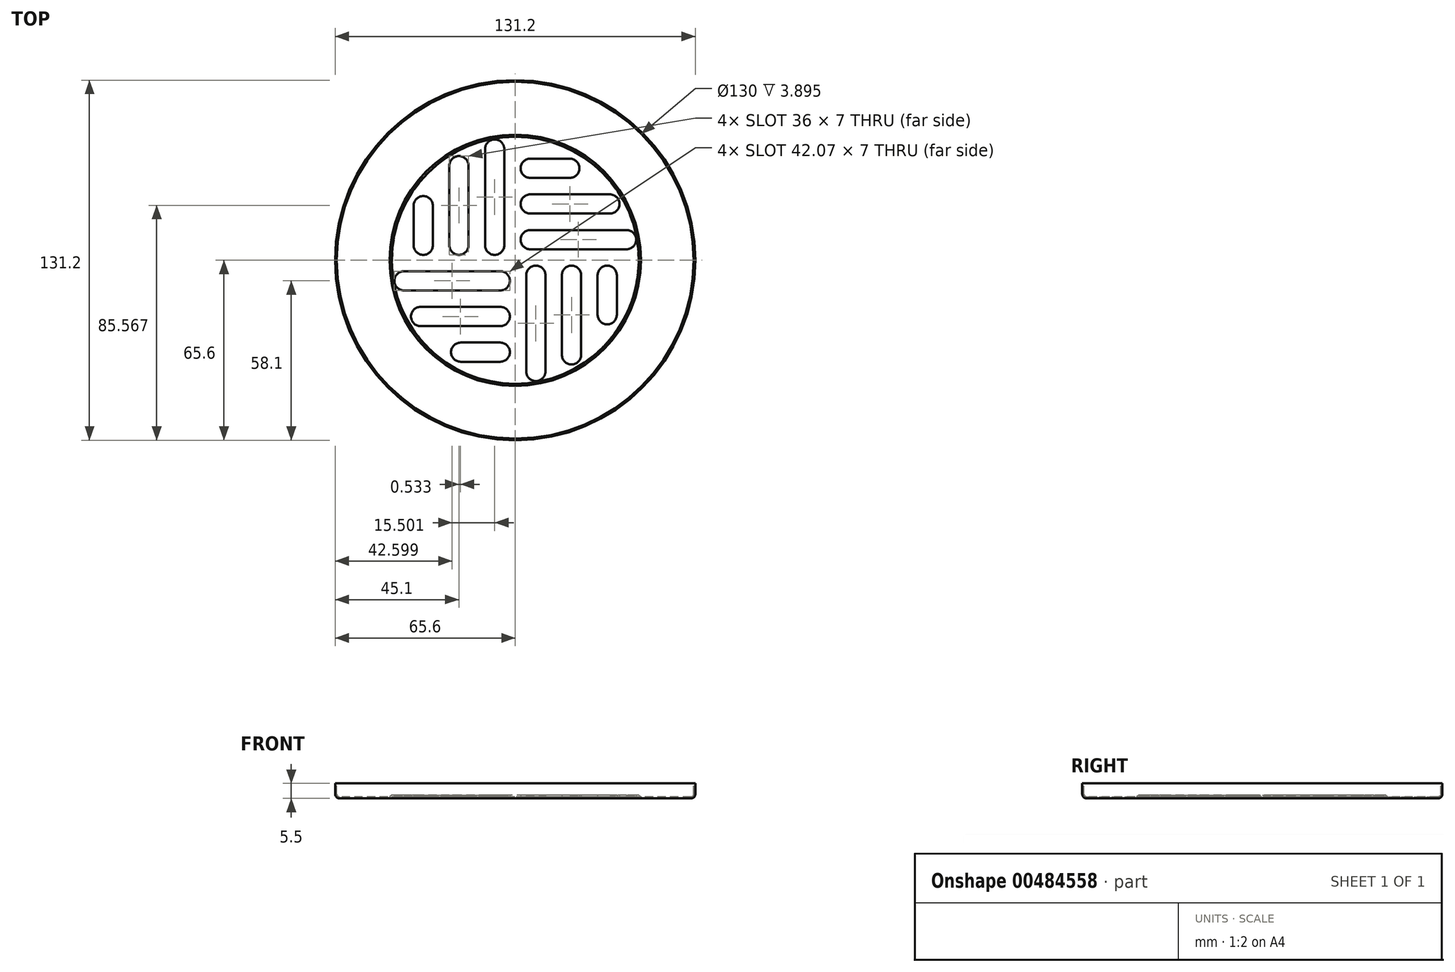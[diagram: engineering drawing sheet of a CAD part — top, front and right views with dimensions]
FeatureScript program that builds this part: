
annotation { "Feature Type Name" : "Feature", "Feature Type Description" : "" }
export const myFeature = defineFeature(function(context is Context, id is Id, definition is map)
    precondition{}
    {
        {
            var Q0;
            Q0=qCreatedBy(makeId("Front.planeOp"),FACE);
            var sketch = newSketch(context, id + "F0", { "sketchPlane" : qUnion([Q0])});
            skLineSegment(sketch, "E0", {"start": v(-65, 4.9) * mm, "end": v(-65, 1) * mm});
            skLineSegment(sketch, "E1", {"start": v(-64, 0) * mm, "end": v(-45.79, 0) * mm});
            skLineSegment(sketch, "E2", {"start": v(-45.79, 0) * mm, "end": v(-45, 0.6) * mm});
            skLineSegment(sketch, "E3", {"start": v(-45, 0.6) * mm, "end": v(0, 0.6) * mm});
            skPoint(sketch, "E4.visualSharp", {"position": v(-65, 0) * mm});
            skArc(sketch, "E4.filletArc", {"start": v(-65, 1) * mm, "mid": v(-64.7, 0.3) * mm, "end": v(-64, 0) * mm});
            skLineSegment(sketch, "E5.0", {"start": v(-44.8, 0) * mm, "end": v(0, 0) * mm});
            skLineSegment(sketch, "E5.1", {"start": v(-65.6, 4.9) * mm, "end": v(-65.6, 1) * mm});
            skArc(sketch, "E5.2", {"start": v(-65.6, 1) * mm, "mid": v(-65.13, -0.13) * mm, "end": v(-64, -0.6) * mm});
            skLineSegment(sketch, "E5.3", {"start": v(-64, -0.6) * mm, "end": v(-45.58, -0.6) * mm});
            skLineSegment(sketch, "E5.4", {"start": v(-45.58, -0.6) * mm, "end": v(-44.8, 0) * mm});
            skLineSegment(sketch, "E6", {"start": v(-65.6, 4.9) * mm, "end": v(-65, 4.9) * mm});
            skLineSegment(sketch, "E7", {"start": v(0, 0) * mm, "end": v(0, 0.6) * mm});
            skLineSegment(sketch, "E8", {"start": v(0, 16) * mm, "end": v(0, -11.03) * mm, "construction": true});
            skSolve(sketch);
        }
        {
            var Q0;
            Q0=makeQuery(id+"F0.imprint","IMPRINT",FACE,{"disambiguationData":[TD([[makeQuery(id+"F0.imprint","IMPRINT",EDGE,{"derivedFrom":sQuery(id+"F0.wireOp",EDGE,"E0")}),-1.0]])]});
            var Q1;
            Q1=sQuery(id+"F0.wireOp",EDGE,"E8");
            revolve(context, id + "F1", {"entities" : qUnion([Q0]), "axis" : qUnion([Q1]), "revolveType" : RevolveType.FULL});
        }
        {
            var Q0;
            Q0=qCreatedBy(makeId("Top.planeOp"),FACE);
            var sketch = newSketch(context, id + "F2", { "sketchPlane" : qUnion([Q0])});
            skLineSegment(sketch, "E9.left", {"start": v(-11, 40.53) * mm, "end": v(-11, 5.47) * mm});
            skLineSegment(sketch, "E9.right", {"start": v(-4, 40.47) * mm, "end": v(-4, 5.47) * mm});
            skLineSegment(sketch, "E10.left", {"start": v(-24, 34.47) * mm, "end": v(-24, 5.47) * mm});
            skLineSegment(sketch, "E10.right", {"start": v(-17, 34.47) * mm, "end": v(-17, 5.47) * mm});
            skLineSegment(sketch, "E11.left", {"start": v(-37, 19.87) * mm, "end": v(-37, 5.47) * mm});
            skLineSegment(sketch, "E11.right", {"start": v(-30, 19.87) * mm, "end": v(-30, 5.47) * mm});
            skArc(sketch, "E12", {"start": v(-37, 19.87) * mm, "mid": v(-33.5, 23.37) * mm, "end": v(-30, 19.87) * mm});
            skArc(sketch, "E13", {"start": v(-30, 5.47) * mm, "mid": v(-33.5, 1.97) * mm, "end": v(-37, 5.47) * mm});
            skArc(sketch, "E14", {"start": v(-24, 5.47) * mm, "mid": v(-20.5, 1.97) * mm, "end": v(-17, 5.47) * mm});
            skArc(sketch, "E15", {"start": v(-17, 34.47) * mm, "mid": v(-20.5, 37.97) * mm, "end": v(-24, 34.47) * mm});
            skArc(sketch, "E16", {"start": v(-11, 40.53) * mm, "mid": v(-7.47, 44.03) * mm, "end": v(-4, 40.47) * mm});
            skArc(sketch, "E17", {"start": v(-11, 5.47) * mm, "mid": v(-7.5, 1.97) * mm, "end": v(-4, 5.47) * mm});
            skLineSegment(sketch, "E18.1.0", {"start": v(-40.47, -4) * mm, "end": v(-5.47, -4) * mm});
            skArc(sketch, "E18.1.1", {"start": v(-5.47, -11) * mm, "mid": v(-1.97, -7.5) * mm, "end": v(-5.47, -4) * mm});
            skLineSegment(sketch, "E18.1.2", {"start": v(-40.53, -11) * mm, "end": v(-5.47, -11) * mm});
            skArc(sketch, "E18.1.3", {"start": v(-40.53, -11) * mm, "mid": v(-44.03, -7.47) * mm, "end": v(-40.47, -4) * mm});
            skLineSegment(sketch, "E18.1.4", {"start": v(-34.47, -17) * mm, "end": v(-5.47, -17) * mm});
            skArc(sketch, "E18.1.5", {"start": v(-34.47, -17) * mm, "mid": v(-37.97, -20.5) * mm, "end": v(-34.47, -24) * mm});
            skLineSegment(sketch, "E18.1.6", {"start": v(-34.47, -24) * mm, "end": v(-5.47, -24) * mm});
            skArc(sketch, "E18.1.7", {"start": v(-5.47, -24) * mm, "mid": v(-1.97, -20.5) * mm, "end": v(-5.47, -17) * mm});
            skLineSegment(sketch, "E18.1.8", {"start": v(-19.87, -30) * mm, "end": v(-5.47, -30) * mm});
            skArc(sketch, "E18.1.9", {"start": v(-19.87, -37) * mm, "mid": v(-23.37, -33.5) * mm, "end": v(-19.87, -30) * mm});
            skLineSegment(sketch, "E18.1.10", {"start": v(-19.87, -37) * mm, "end": v(-5.47, -37) * mm});
            skArc(sketch, "E18.1.11", {"start": v(-5.47, -30) * mm, "mid": v(-1.97, -33.5) * mm, "end": v(-5.47, -37) * mm});
            skLineSegment(sketch, "E18.2.0", {"start": v(4, -40.47) * mm, "end": v(4, -5.47) * mm});
            skArc(sketch, "E18.2.1", {"start": v(11, -5.47) * mm, "mid": v(7.5, -1.97) * mm, "end": v(4, -5.47) * mm});
            skLineSegment(sketch, "E18.2.2", {"start": v(11, -40.53) * mm, "end": v(11, -5.47) * mm});
            skArc(sketch, "E18.2.3", {"start": v(11, -40.53) * mm, "mid": v(7.47, -44.03) * mm, "end": v(4, -40.47) * mm});
            skLineSegment(sketch, "E18.2.4", {"start": v(17, -34.47) * mm, "end": v(17, -5.47) * mm});
            skArc(sketch, "E18.2.5", {"start": v(17, -34.47) * mm, "mid": v(20.5, -37.97) * mm, "end": v(24, -34.47) * mm});
            skLineSegment(sketch, "E18.2.6", {"start": v(24, -34.47) * mm, "end": v(24, -5.47) * mm});
            skArc(sketch, "E18.2.7", {"start": v(24, -5.47) * mm, "mid": v(20.5, -1.97) * mm, "end": v(17, -5.47) * mm});
            skLineSegment(sketch, "E18.2.8", {"start": v(30, -19.87) * mm, "end": v(30, -5.47) * mm});
            skArc(sketch, "E18.2.9", {"start": v(37, -19.87) * mm, "mid": v(33.5, -23.37) * mm, "end": v(30, -19.87) * mm});
            skLineSegment(sketch, "E18.2.10", {"start": v(37, -19.87) * mm, "end": v(37, -5.47) * mm});
            skArc(sketch, "E18.2.11", {"start": v(30, -5.47) * mm, "mid": v(33.5, -1.97) * mm, "end": v(37, -5.47) * mm});
            skLineSegment(sketch, "E18.3.0", {"start": v(40.47, 4) * mm, "end": v(5.47, 4) * mm});
            skArc(sketch, "E18.3.1", {"start": v(5.47, 11) * mm, "mid": v(1.97, 7.5) * mm, "end": v(5.47, 4) * mm});
            skLineSegment(sketch, "E18.3.2", {"start": v(40.53, 11) * mm, "end": v(5.47, 11) * mm});
            skArc(sketch, "E18.3.3", {"start": v(40.53, 11) * mm, "mid": v(44.03, 7.47) * mm, "end": v(40.47, 4) * mm});
            skLineSegment(sketch, "E18.3.4", {"start": v(34.47, 17) * mm, "end": v(5.47, 17) * mm});
            skArc(sketch, "E18.3.5", {"start": v(34.47, 17) * mm, "mid": v(37.97, 20.5) * mm, "end": v(34.47, 24) * mm});
            skLineSegment(sketch, "E18.3.6", {"start": v(34.47, 24) * mm, "end": v(5.47, 24) * mm});
            skArc(sketch, "E18.3.7", {"start": v(5.47, 24) * mm, "mid": v(1.97, 20.5) * mm, "end": v(5.47, 17) * mm});
            skLineSegment(sketch, "E18.3.8", {"start": v(19.87, 30) * mm, "end": v(5.47, 30) * mm});
            skArc(sketch, "E18.3.9", {"start": v(19.87, 37) * mm, "mid": v(23.37, 33.5) * mm, "end": v(19.87, 30) * mm});
            skLineSegment(sketch, "E18.3.10", {"start": v(19.87, 37) * mm, "end": v(5.47, 37) * mm});
            skArc(sketch, "E18.3.11", {"start": v(5.47, 30) * mm, "mid": v(1.97, 33.5) * mm, "end": v(5.47, 37) * mm});
            skPoint(sketch, "E18.center", {"position": v(0, 0) * mm});
            skSolve(sketch);
        }
        {
            var Q0;
            Q0=makeQuery(id+"F2.imprint","IMPRINT",FACE,{"disambiguationData":[TD([[makeQuery(id+"F2.imprint","IMPRINT",EDGE,{"derivedFrom":sQuery(id+"F2.wireOp",EDGE,"E18.1.0")}),-1.0]])]});
            var Q1;
            Q1=makeQuery(id+"F2.imprint","IMPRINT",FACE,{"disambiguationData":[TD([[makeQuery(id+"F2.imprint","IMPRINT",EDGE,{"derivedFrom":sQuery(id+"F2.wireOp",EDGE,"E18.1.4")}),-1.0]])]});
            var Q2;
            Q2=makeQuery(id+"F2.imprint","IMPRINT",FACE,{"disambiguationData":[TD([[makeQuery(id+"F2.imprint","IMPRINT",EDGE,{"derivedFrom":sQuery(id+"F2.wireOp",EDGE,"E18.1.8")}),-1.0]])]});
            var Q3;
            Q3=makeQuery(id+"F2.imprint","IMPRINT",FACE,{"disambiguationData":[TD([[makeQuery(id+"F2.imprint","IMPRINT",EDGE,{"derivedFrom":sQuery(id+"F2.wireOp",EDGE,"E11.left")}),1.0]])]});
            var Q4;
            Q4=makeQuery(id+"F2.imprint","IMPRINT",FACE,{"disambiguationData":[TD([[makeQuery(id+"F2.imprint","IMPRINT",EDGE,{"derivedFrom":sQuery(id+"F2.wireOp",EDGE,"E10.left")}),1.0]])]});
            var Q5;
            Q5=makeQuery(id+"F2.imprint","IMPRINT",FACE,{"disambiguationData":[TD([[makeQuery(id+"F2.imprint","IMPRINT",EDGE,{"derivedFrom":sQuery(id+"F2.wireOp",EDGE,"E9.left")}),1.0]])]});
            var Q6;
            Q6=makeQuery(id+"F2.imprint","IMPRINT",FACE,{"disambiguationData":[TD([[makeQuery(id+"F2.imprint","IMPRINT",EDGE,{"derivedFrom":sQuery(id+"F2.wireOp",EDGE,"E18.2.4")}),-1.0]])]});
            var Q7;
            Q7=makeQuery(id+"F2.imprint","IMPRINT",FACE,{"disambiguationData":[TD([[makeQuery(id+"F2.imprint","IMPRINT",EDGE,{"derivedFrom":sQuery(id+"F2.wireOp",EDGE,"E18.2.0")}),-1.0]])]});
            var Q8;
            Q8=makeQuery(id+"F2.imprint","IMPRINT",FACE,{"disambiguationData":[TD([[makeQuery(id+"F2.imprint","IMPRINT",EDGE,{"derivedFrom":sQuery(id+"F2.wireOp",EDGE,"E18.2.8")}),-1.0]])]});
            var Q9;
            Q9=makeQuery(id+"F2.imprint","IMPRINT",FACE,{"disambiguationData":[TD([[makeQuery(id+"F2.imprint","IMPRINT",EDGE,{"derivedFrom":sQuery(id+"F2.wireOp",EDGE,"E18.3.0")}),-1.0]])]});
            var Q10;
            Q10=makeQuery(id+"F2.imprint","IMPRINT",FACE,{"disambiguationData":[TD([[makeQuery(id+"F2.imprint","IMPRINT",EDGE,{"derivedFrom":sQuery(id+"F2.wireOp",EDGE,"E18.3.4")}),-1.0]])]});
            var Q11;
            Q11=makeQuery(id+"F2.imprint","IMPRINT",FACE,{"disambiguationData":[TD([[makeQuery(id+"F2.imprint","IMPRINT",EDGE,{"derivedFrom":sQuery(id+"F2.wireOp",EDGE,"E18.3.8")}),-1.0]])]});
            extrude(context, id + "F3", {"entities" : qUnion([Q0, Q1, Q2, Q3, Q4, Q5, Q6, Q7, Q8, Q9, Q10, Q11]), "operationType" : NewBodyOperationType.REMOVE, "endBound" : BoundingType.THROUGH_ALL, "depth" : 0.7 * mm});
        }
    });
